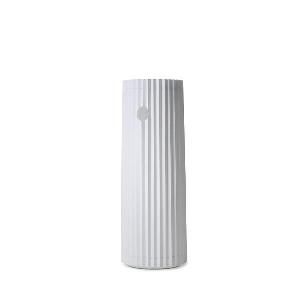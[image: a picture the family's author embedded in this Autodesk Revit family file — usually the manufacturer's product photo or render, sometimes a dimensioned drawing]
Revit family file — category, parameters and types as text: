
# Revit family: vivaa_social_-_vss_7000_vtl_d_ws_1596mm_rws_00816382_a41b
name_source: partatom
category: Lighting Fixtures
units: mm (PartAtom-declared; Revit-internal decimal feet)

## family parameters
Cut with Voids When Loaded = No
Host = Face
Light Source = No
Part Type = Normal
Room Calculation Point = No
Round Connector Dimension = Use Diameter
Shared = No

## types (1)
- VIVAA.social - VSS 7000/VTL/D/WS/1596MM/RWS (1 x LED, 6850 lm, 2700-6500K)
    Apparent Load = 79 VA
    Approval mark = CE
    CIE Flux Codes = 31 55 78 19 100
    Color Rendering = 90-100
    Color Temperature = 2700-6500K
    Control Gear = Electronic ballast
    Default Elevation = 1800 mm
    Description = VSS 7000/VTL/D|Free-standing luminaire|light source:     |work equipment: Electronic ballast|light distribution: Direct/indirect|direct ratio: approx. 19 %|technology: Continuously dimmable|operation: Pull cord|luminaire body|material: glass fiber/cellulose|surface: Untreated|colour: Nature|lamp cover: Polycarbonate (PC), Satine|tubular section|material: Steel tube|surface: Painted|Form: Tubular section upright|colour of tubular section: Pure white|luminaire base|Form: Round (flat)|mains lead: 2.20 m Mains plug CEE 7/VII|Fastening: Floor standing base|glare control: Diffusor|
    Frequency = 60 Hz
    Height = 1596 mm
    Lamp = 1 x LED
    Lamp Light Flux = 6850 lm
    Lamp count = 1
    Length = 609 mm
    Luminous efficacy = 87 lm/W
    Manufacturer = Waldmann
    ModVariant = No
    Model = 00816382
    Mounting Place = Floor
    Mounting Type = Freestanding
    Number of Poles = 1
    OnlyDefault = Yes
    Power Factor = 1
    Product Name = VIVAA.social - VSS 7000/VTL/D/WS/1596MM/RWS
    Product group = Free standing luminaire
    ProductGroupID = 13
    Protection Class = Protection class I
    Protection Degree = IP 20
    RLX_Detail_Level = 1
    RLX_Emergency_Light_Flux = 0 lm
    RLX_Emergency_Type = 0
    RLX_Emergency_Type_DB = No
    RlxData = <blob elided: 72725 chars, md5=1e97c559>
    Socket = socket
    Standby Power = 0 W
    System Light Flux = 6850 lm
    System Power = 79 W
    Type Comments = Product without accessories
    Type Image = vivaasocial_weiss_lang-oschirm.jpg
    URL = http://relux.com
    VarID = ---
    Voltage = 230 V
    Voltage Range = 220-240 V
    Weight = 0.00 kg
    Width = 0 mm  [stored 0 ft]

note: [stored X ft] marks values corroborated as IEEE doubles in the binary element streams (Revit-internal decimal feet)

## geometry (parser evidence)
native form markers: Blend x4, Sweep x14
no freeform markers — native parametric forms only
